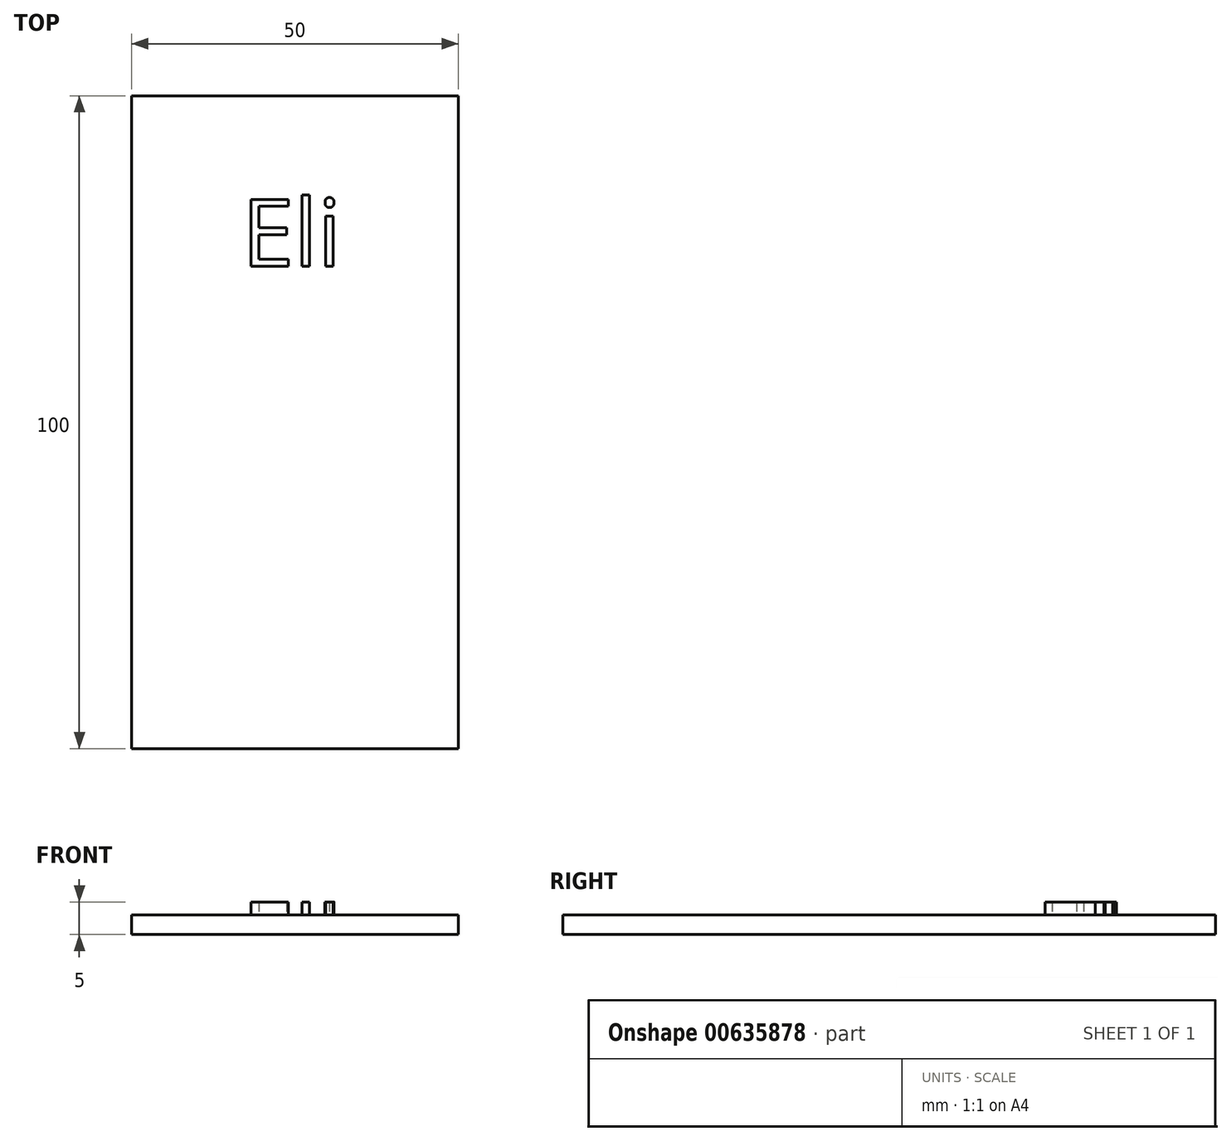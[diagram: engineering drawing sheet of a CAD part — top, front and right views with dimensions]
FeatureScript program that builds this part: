
annotation { "Feature Type Name" : "Feature", "Feature Type Description" : "" }
export const myFeature = defineFeature(function(context is Context, id is Id, definition is map)
    precondition{}
    {
        {
            var Q0;
            Q0=qCreatedBy(makeId("Top.planeOp"),FACE);
            var sketch = newSketch(context, id + "F0", { "sketchPlane" : qUnion([Q0])});
            skLineSegment(sketch, "E0.bottom", {"start": v(-25, -50) * mm, "end": v(25, -50) * mm});
            skLineSegment(sketch, "E0.top", {"start": v(-25, 50) * mm, "end": v(25, 50) * mm});
            skLineSegment(sketch, "E0.left", {"start": v(-25, -50) * mm, "end": v(-25, 50) * mm});
            skLineSegment(sketch, "E0.right", {"start": v(25, -50) * mm, "end": v(25, 50) * mm});
            skPoint(sketch, "E0.middle", {"position": v(0, 0) * mm});
            skSolve(sketch);
        }
        {
            var Q0;
            Q0=makeQuery(id+"F0.imprint","IMPRINT",FACE,{"disambiguationData":[TD([[makeQuery(id+"F0.imprint","IMPRINT",EDGE,{"derivedFrom":sQuery(id+"F0.wireOp",EDGE,"E0.bottom")}),1.0]])]});
            extrude(context, id + "F1", {"entities" : qUnion([Q0]), "depth" : 3 * mm, "offsetDistance" : 25 * mm});
        }
        {
            var Q0;
            Q0=makeQuery(id+"F1.opExtrude","CAP_FACE",FACE,{"disambiguationData":[OSD([sQuery(id+"F0.wireOp",EDGE,"E0.bottom"),sQuery(id+"F0.wireOp",EDGE,"E0.top"),sQuery(id+"F0.wireOp",EDGE,"E0.left"),sQuery(id+"F0.wireOp",EDGE,"E0.right")])],"isStart":false});
            var sketch = newSketch(context, id + "F2", { "sketchPlane" : qUnion([Q0])});
            skText(sketch, "E1", { "text": "Eli", "fontName": "OpenSans-Regular.ttf"});
            const initialGuessF2  = {"E1": [-0.00814, 0.02389, 1, 0, 0.01033]};
            skSetInitialGuess(sketch, initialGuessF2);
            skSolve(sketch);
        }
        {
            var Q0;
            Q0 = qSketchRegion(id + "F2", true);
            extrude(context, id + "F3", {"entities" : qUnion([Q0]), "operationType" : NewBodyOperationType.ADD, "depth" : 2 * mm, "offsetDistance" : 25 * mm});
        }
    });
